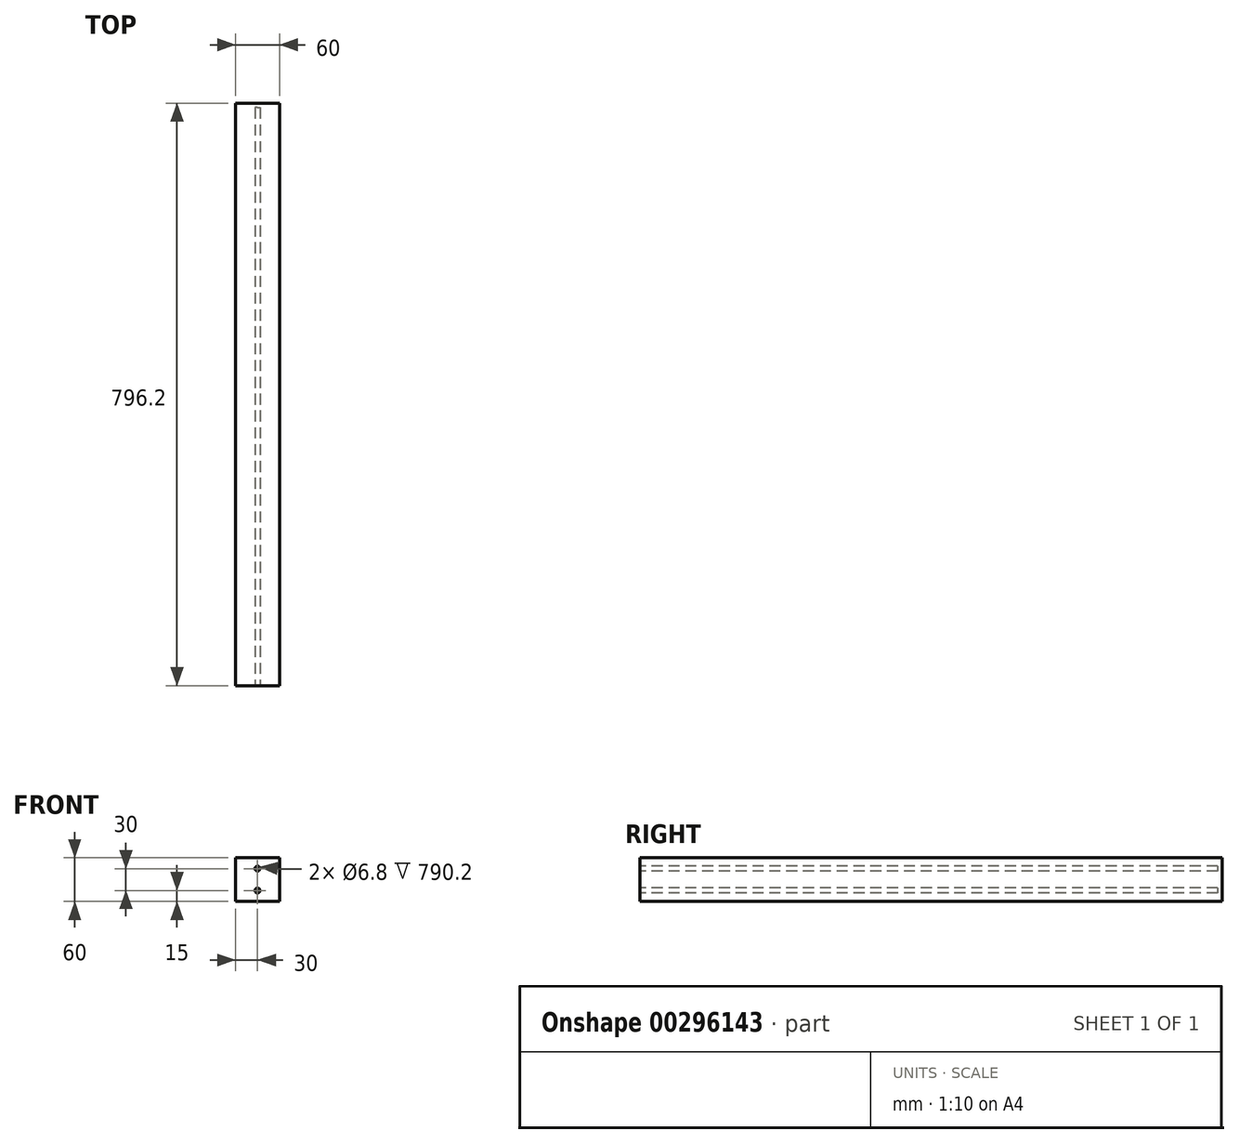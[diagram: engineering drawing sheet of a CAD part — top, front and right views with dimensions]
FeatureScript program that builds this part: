
annotation { "Feature Type Name" : "Feature", "Feature Type Description" : "" }
export const myFeature = defineFeature(function(context is Context, id is Id, definition is map)
    precondition{}
    {
        {
            var Q0;
            Q0=qCreatedBy(makeId("Front.planeOp"),FACE);
            var sketch = newSketch(context, id + "F0", { "sketchPlane" : qUnion([Q0])});
            skLineSegment(sketch, "E0.bottom", {"start": v(30, 30) * mm, "end": v(-30, 30) * mm});
            skLineSegment(sketch, "E0.top", {"start": v(30, -30) * mm, "end": v(-30, -30) * mm});
            skLineSegment(sketch, "E0.left", {"start": v(30, 30) * mm, "end": v(30, -30) * mm});
            skLineSegment(sketch, "E0.right", {"start": v(-30, 30) * mm, "end": v(-30, -30) * mm});
            skPoint(sketch, "E0.middle", {"position": v(0, 0) * mm});
            skSolve(sketch);
        }
        {
            var Q0;
            Q0 = qSketchRegion(id + "F0", true);
            extrude(context, id + "F1", {"entities" : qUnion([Q0]), "depth" : 796.2 * mm});
        }
        {
            var Q0;
            Q0=makeQuery(id+"F1.opExtrude","CAP_FACE",FACE,{"disambiguationData":[OSD([sQuery(id+"F0.wireOp",EDGE,"E0.bottom"),sQuery(id+"F0.wireOp",EDGE,"E0.top"),sQuery(id+"F0.wireOp",EDGE,"E0.left"),sQuery(id+"F0.wireOp",EDGE,"E0.right")])],"isStart":false});
            var sketch = newSketch(context, id + "F2", { "sketchPlane" : qUnion([Q0])});
            skLineSegment(sketch, "E1.bottom", {"start": v(-30, 30) * mm, "end": v(30, 30) * mm});
            skLineSegment(sketch, "E1.top", {"start": v(-30, -30) * mm, "end": v(30, -30) * mm});
            skLineSegment(sketch, "E1.left", {"start": v(-30, 30) * mm, "end": v(-30, -30) * mm});
            skLineSegment(sketch, "E1.right", {"start": v(30, 30) * mm, "end": v(30, -30) * mm});
            skSolve(sketch);
        }
        {
            var Q0;
            Q0 = qSketchRegion(id + "F2", true);
            extrude(context, id + "F3", {"entities" : qUnion([Q0]), "operationType" : NewBodyOperationType.ADD, "oppositeDirection" : true, "depth" : 6 * mm});
        }
        {
            var Q0;
            Q0=makeQuery(id+"F1.opExtrude","CAP_FACE",FACE,{"disambiguationData":[OSD([sQuery(id+"F0.wireOp",EDGE,"E0.bottom"),sQuery(id+"F0.wireOp",EDGE,"E0.top"),sQuery(id+"F0.wireOp",EDGE,"E0.left"),sQuery(id+"F0.wireOp",EDGE,"E0.right")])],"isStart":false});
            var sketch = newSketch(context, id + "F4", { "sketchPlane" : qUnion([Q0])});
            skLineSegment(sketch, "E2", {"start": v(0, 30) * mm, "end": v(0, 15) * mm, "construction": true});
            skPoint(sketch, "E2.endSnap0", {"position": v(0, 30) * mm});
            skLineSegment(sketch, "E3", {"start": v(0, -30) * mm, "end": v(0, -15) * mm, "construction": true});
            skPoint(sketch, "E3.endSnap0", {"position": v(0, -30) * mm});
            skCircle(sketch, "E4", {"center": v(0, 15) * mm, "radius": 3.4 * mm});
            skCircle(sketch, "E5", {"center": v(0, -15) * mm, "radius": 3.4 * mm});
            skSolve(sketch);
        }
        {
            var Q0;
            Q0=makeQuery(id+"F4.imprint","IMPRINT",FACE,{"disambiguationData":[TD([[makeQuery(id+"F4.imprint","IMPRINT",EDGE,{"derivedFrom":sQuery(id+"F4.wireOp",EDGE,"E4")}),1.0]])]});
            var Q1;
            Q1=makeQuery(id+"F4.imprint","IMPRINT",FACE,{"disambiguationData":[TD([[makeQuery(id+"F4.imprint","IMPRINT",EDGE,{"derivedFrom":sQuery(id+"F4.wireOp",EDGE,"E5")}),1.0]])]});
            extrude(context, id + "F5", {"entities" : qUnion([Q0, Q1]), "operationType" : NewBodyOperationType.REMOVE, "endBound" : BoundingType.THROUGH_ALL, "oppositeDirection" : true, "depth" : 25 * mm});
        }
        {
            var Q0;
            Q0=makeQuery(id+"F1.opExtrude","CAP_FACE",FACE,{"disambiguationData":[OSD([sQuery(id+"F0.wireOp",EDGE,"E0.bottom"),sQuery(id+"F0.wireOp",EDGE,"E0.top"),sQuery(id+"F0.wireOp",EDGE,"E0.left"),sQuery(id+"F0.wireOp",EDGE,"E0.right")])],"isStart":true});
            var sketch = newSketch(context, id + "F6", { "sketchPlane" : qUnion([Q0])});
            skLineSegment(sketch, "E6.bottom", {"start": v(-30, 30) * mm, "end": v(30, 30) * mm});
            skLineSegment(sketch, "E6.top", {"start": v(-30, -30) * mm, "end": v(30, -30) * mm});
            skLineSegment(sketch, "E6.left", {"start": v(-30, 30) * mm, "end": v(-30, -30) * mm});
            skLineSegment(sketch, "E6.right", {"start": v(30, 30) * mm, "end": v(30, -30) * mm});
            skSolve(sketch);
        }
        {
            var Q0;
            Q0 = qSketchRegion(id + "F6", true);
            extrude(context, id + "F7", {"entities" : qUnion([Q0]), "operationType" : NewBodyOperationType.ADD, "oppositeDirection" : true, "depth" : 6 * mm});
        }
    });
